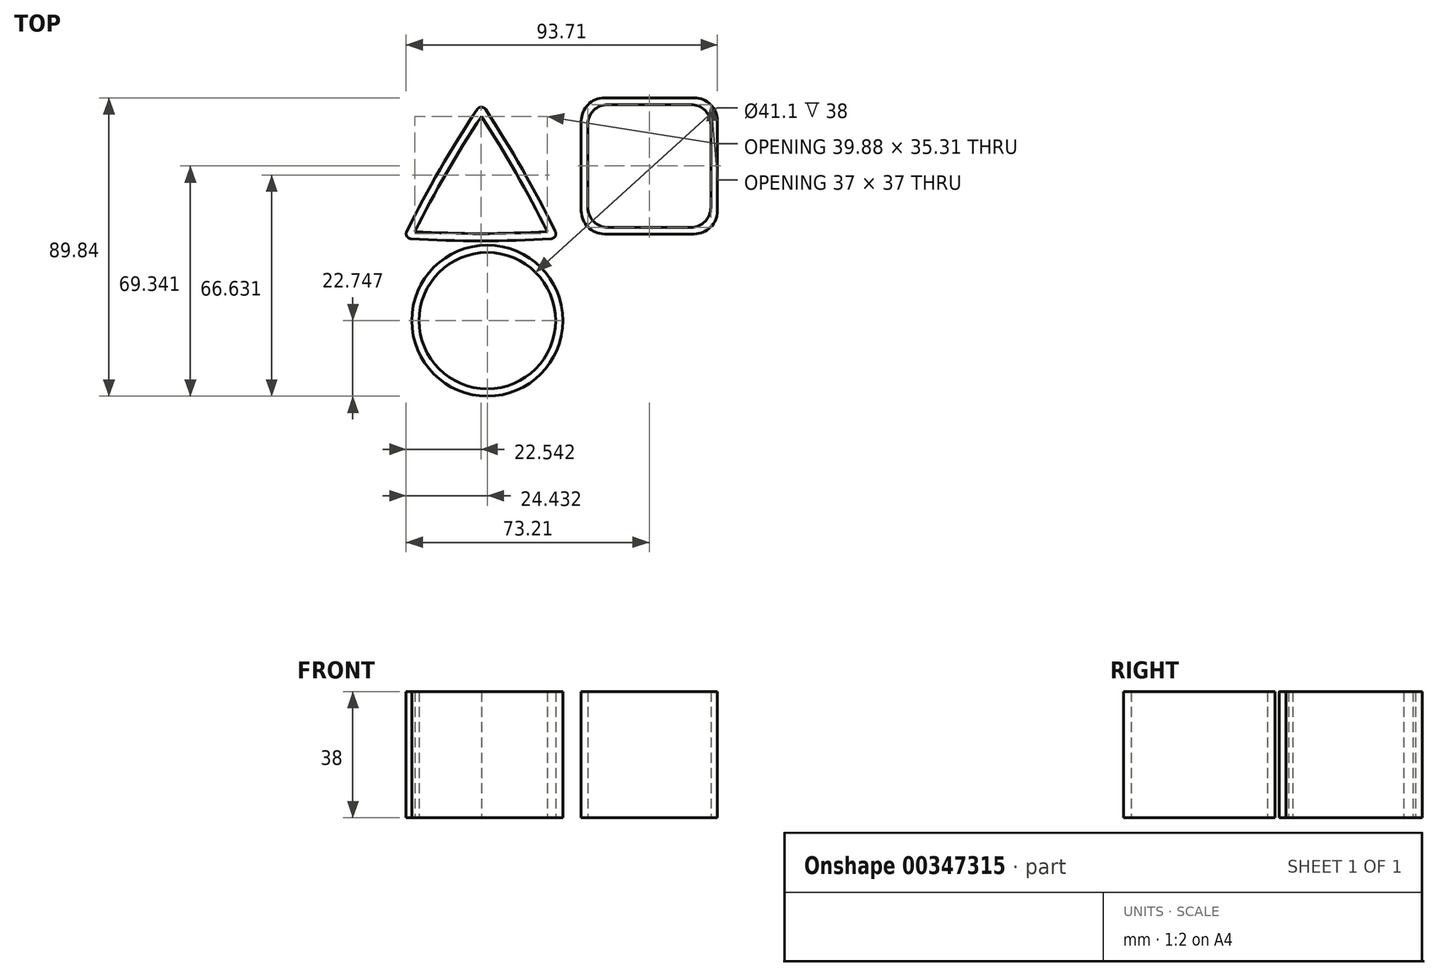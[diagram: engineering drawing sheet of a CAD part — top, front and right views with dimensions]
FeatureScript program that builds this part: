
annotation { "Feature Type Name" : "Feature", "Feature Type Description" : "" }
export const myFeature = defineFeature(function(context is Context, id is Id, definition is map)
    precondition{}
    {
        {
            var Q0;
            Q0=qCreatedBy(makeId("Top.planeOp"),FACE);
            var sketch = newSketch(context, id + "F0", { "sketchPlane" : qUnion([Q0])});
            skLineSegment(sketch, "E0.bottom", {"start": v(7, 2) * mm, "end": v(34, 2) * mm});
            skLineSegment(sketch, "E0.left", {"start": v(0, 9) * mm, "end": v(0, 22.5) * mm});
            skLineSegment(sketch, "E0.right", {"start": v(41, 9) * mm, "end": v(41, 36) * mm});
            skLineSegment(sketch, "E1.top", {"start": v(33, 4) * mm, "end": v(8, 4) * mm});
            skLineSegment(sketch, "E1.left", {"start": v(39, 35) * mm, "end": v(39, 10) * mm});
            skPoint(sketch, "E1.middle", {"position": v(20.5, 22.5) * mm});
            skPoint(sketch, "E1.middle.positionSnap0", {"position": v(0, 22.5) * mm});
            skPoint(sketch, "E1.middle.positionSnap1", {"position": v(20.5, 2) * mm});
            skPoint(sketch, "E1.centerSnap0", {"position": v(0, 22.5) * mm});
            skPoint(sketch, "E1.centerSnap1", {"position": v(20.5, 2) * mm});
            skPoint(sketch, "E2.visualSharp", {"position": v(2, 41) * mm});
            skPoint(sketch, "E3.visualSharp", {"position": v(0, 43) * mm});
            skLineSegment(sketch, "E4", {"start": v(0, 22.5) * mm, "end": v(0, 36) * mm});
            skLineSegment(sketch, "E5", {"start": v(34, 43) * mm, "end": v(7, 43) * mm});
            skLineSegment(sketch, "E6", {"start": v(33, 41) * mm, "end": v(8, 41) * mm});
            skLineSegment(sketch, "E7", {"start": v(2, 10) * mm, "end": v(2, 35) * mm});
            skArc(sketch, "E8.filletArc", {"start": v(8, 41) * mm, "mid": v(3.76, 39.23) * mm, "end": v(2, 35) * mm});
            skPoint(sketch, "E9.visualSharp", {"position": v(39, 41) * mm});
            skArc(sketch, "E9.filletArc", {"start": v(39, 35) * mm, "mid": v(37.24, 39.23) * mm, "end": v(33, 41) * mm});
            skPoint(sketch, "E10.visualSharp", {"position": v(39, 4) * mm});
            skArc(sketch, "E10.filletArc", {"start": v(33, 4) * mm, "mid": v(37.24, 5.75) * mm, "end": v(39, 10) * mm});
            skPoint(sketch, "E11.visualSharp", {"position": v(2, 4) * mm});
            skArc(sketch, "E11.filletArc", {"start": v(2, 10) * mm, "mid": v(3.76, 5.75) * mm, "end": v(8, 4) * mm});
            skArc(sketch, "E12.filletArc", {"start": v(7, 43) * mm, "mid": v(2.05, 40.94) * mm, "end": v(0, 36) * mm});
            skPoint(sketch, "E13.visualSharp", {"position": v(41, 43) * mm});
            skArc(sketch, "E13.filletArc", {"start": v(41, 36) * mm, "mid": v(38.95, 40.94) * mm, "end": v(34, 43) * mm});
            skPoint(sketch, "E14.visualSharp", {"position": v(41, 2) * mm});
            skArc(sketch, "E14.filletArc", {"start": v(34, 2) * mm, "mid": v(38.95, 4.04) * mm, "end": v(41, 9) * mm});
            skPoint(sketch, "E15.visualSharp", {"position": v(0, 2) * mm});
            skArc(sketch, "E15.filletArc", {"start": v(0, 9) * mm, "mid": v(2.05, 4.04) * mm, "end": v(7, 2) * mm});
            skSolve(sketch);
        }
        {
            var Q0;
            Q0 = qSketchRegion(id + "F0", true);
            extrude(context, id + "F1", {"entities" : qUnion([Q0]), "depth" : 38 * mm});
        }
        {
            var Q0;
            Q0=qCreatedBy(makeId("Top.planeOp"),FACE);
            var sketch = newSketch(context, id + "F2", { "sketchPlane" : qUnion([Q0])});
            skCircle(sketch, "E16", {"center": v(-28.28, -24.1) * mm, "radius": 22.75 * mm});
            skCircle(sketch, "E17", {"center": v(-28.28, -24.1) * mm, "radius": 20.55 * mm});
            skSolve(sketch);
        }
        {
            var Q0;
            Q0 = qSketchRegion(id + "F2", true);
            extrude(context, id + "F3", {"entities" : qUnion([Q0]), "depth" : 38 * mm});
        }
        {
            var Q0;
            Q0=qCreatedBy(makeId("Top.planeOp"),FACE);
            var sketch = newSketch(context, id + "F4", { "sketchPlane" : qUnion([Q0])});
            skPoint(sketch, "E18.visualSharp", {"position": v(-30.05, 41.42) * mm});
            skPoint(sketch, "E19.visualSharp", {"position": v(-53.55, 0.72) * mm});
            skPoint(sketch, "E20.visualSharp", {"position": v(-6.8, 0.72) * mm});
            skArc(sketch, "E21", {"start": v(-31.3, 39.54) * mm, "mid": v(-42.5, 21.47) * mm, "end": v(-52.55, 2.74) * mm});
            skArc(sketch, "E22", {"start": v(-51.3, 0.57) * mm, "mid": v(-30.17, -0.07) * mm, "end": v(-9.04, 0.57) * mm});
            skArc(sketch, "E23", {"start": v(-7.79, 2.73) * mm, "mid": v(-17.73, 21.46) * mm, "end": v(-28.8, 39.53) * mm});
            skArc(sketch, "E24.filletArc", {"start": v(-28.8, 39.53) * mm, "mid": v(-30.05, 40.21) * mm, "end": v(-31.3, 39.54) * mm});
            skArc(sketch, "E25.filletArc", {"start": v(-52.55, 2.74) * mm, "mid": v(-52.5, 1.32) * mm, "end": v(-51.3, 0.57) * mm});
            skArc(sketch, "E26.filletArc", {"start": v(-9.04, 0.57) * mm, "mid": v(-7.84, 1.32) * mm, "end": v(-7.79, 2.73) * mm});
            skSolve(sketch);
        }
        {
            var Q0;
            Q0 = qSketchRegion(id + "F4", true);
            extrude(context, id + "F5", {"entities" : qUnion([Q0]), "depth" : 38 * mm});
        }
        {
            var Q0;
            Q0=makeQuery(id+"F5.opExtrude","CAP_FACE",FACE,{"disambiguationData":[OSD([sQuery(id+"F4.wireOp",EDGE,"E21"),sQuery(id+"F4.wireOp",EDGE,"E22"),sQuery(id+"F4.wireOp",EDGE,"E23"),sQuery(id+"F4.wireOp",EDGE,"E24.filletArc"),sQuery(id+"F4.wireOp",EDGE,"E25.filletArc"),sQuery(id+"F4.wireOp",EDGE,"E26.filletArc")])],"isStart":false});
            shell(context, id + "F6", {"entities" : qUnion([Q0]), "thickness" : 2.2 * mm});
        }
        {
            var Q0;
            Q0=makeQuery(id+"F6.opShell","OFFSET_FACE",FACE,{"disambiguationData":[OSD([sQuery(id+"F4.wireOp",EDGE,"E21"),sQuery(id+"F4.wireOp",EDGE,"E22"),sQuery(id+"F4.wireOp",EDGE,"E23"),sQuery(id+"F4.wireOp",EDGE,"E24.filletArc"),sQuery(id+"F4.wireOp",EDGE,"E25.filletArc"),sQuery(id+"F4.wireOp",EDGE,"E26.filletArc")])]});
            extrude(context, id + "F7", {"entities" : qUnion([Q0]), "operationType" : NewBodyOperationType.REMOVE, "endBound" : BoundingType.THROUGH_ALL, "oppositeDirection" : true, "depth" : 25 * mm});
        }
    });
